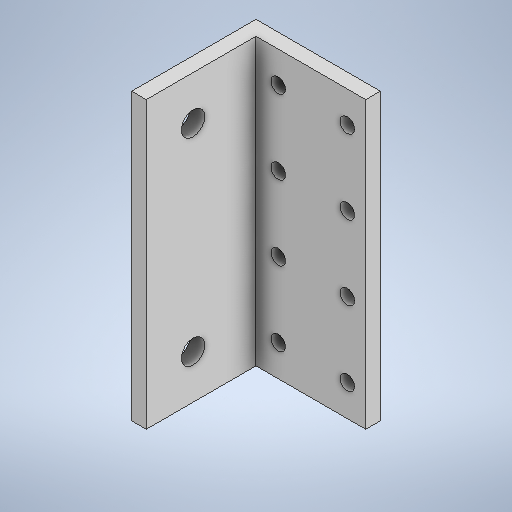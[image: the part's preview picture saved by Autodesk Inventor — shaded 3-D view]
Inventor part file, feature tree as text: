
AUTODESK INVENTOR PART (.ipt)
format: ipt  version: 2025.1 (Build 291241000, 241)  size: 306,688 bytes
history: native  units: in
note: dims shown in document units (in); Inventor stores cm internally (conversion verified against a paired STEP export)
features: extrude x6, sketch x6, direct_edit x3, move_body x3
ambient origin geometry x8: Origin, YZ Plane, XZ Plane, XY Plane, X Axis, Y Axis, Z Axis, Center Point
bodies: Solid1 (feature_tree)
feature tree (18):
  extrude  "Extrusion1"  Depth=1.063in
  extrude  "Extrusion2"  Depth=0.125in
  direct_edit  "Direct Edit1"
  extrude  "Extrusion3"  Depth=0.535in TaperAngle=0.0deg
  direct_edit  "Direct Edit2"
  extrude  "Extrusion4"  Depth=0.315in
  direct_edit  "Direct Edit3"
  extrude  "Extrusion5"  Depth=0.125in
  extrude  "Extrusion6"  Depth=0.125in
  sketch  "Sketch1"  dims[d0=1.063in d1=1.063in]
  sketch  "Sketch2"  dims[d2=0.125in d3=0.125in]
  sketch  "Sketch4"  dims[d4=90.0deg d5=0.535in d6=0.0in]
  sketch  "Sketch5"  dims[d7=0.535in d8=0.315in]
  sketch  "Sketch6"  dims[d9=0.125in d10=0.59in]
  sketch  "Sketch7"  dims[d11=180.0deg d12=0.125in d13=0.635in d14=0.0in d15=0.0in d16=0.0in d17=0.635in d18=0.535in d19=0.315in d20=180.0deg d21=0.125in d22=0.59in d23=0.125in d24=0.535in d25=0.0in d26=0.0in d27=0.0in d28=0.635in d29=0.535in d31=0.315in d32=0.125in d33=0.59in d34=0.125in d35=0.535in d36=0.0in d37=0.0in d38=0.0in d39=0.635in d40=0.535in d41=0.315in d42=0.125in d43=0.59in d44=180.0deg d45=0.125in d46=0.535in d47=0.0in d48=0.4in d49=0.375in d50=90.0deg d51=0.4in d52=0.375in d53=270.0deg d54=0.2in d55=0.2in d56=0.535in d57=0.0in]
  move_body  "Move1"
  move_body  "Move2"
  move_body  "Move3"
